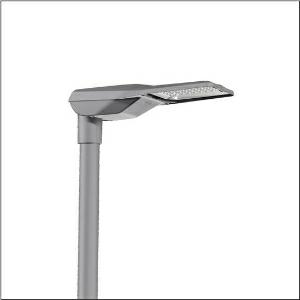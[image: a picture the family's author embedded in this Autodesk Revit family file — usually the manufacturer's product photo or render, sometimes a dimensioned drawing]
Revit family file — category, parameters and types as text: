
# Revit family: streetlight_sl_21_iq_mini___st1_5a_5xe2p31d08gb_fdd6
name_source: partatom
category: Lighting Fixtures
units: mm (PartAtom-declared; Revit-internal decimal feet)

## family parameters
Cut with Voids When Loaded = No
Host = Face
Light Source = No
Part Type = Normal
Room Calculation Point = No
Round Connector Dimension = Use Diameter
Shared = No

## types (1)
- --- (1 x LED, 5580 lm, 37.1 W, 3000K)
    Apparent Load = 37 VA
    CIE Flux Codes = 22 53 95 100 100
    Color Rendering = 70
    Color Temperature = 3000K
    Default Elevation = 1800 mm
    Description = Streetlight SL 21 iQ mini, mast luminaire, primary light control with lens, of PMMA, primary optical cover: cover, of toughened safety glass, transparent, light distribution: ST1.5a, light emission: direct distribution, primary light characteristic: asymmetric, installation type: post-top, side-entry, LED, High Power LED, rated luminous flux: 5.580lm, luminous efficacy: 150lm/W, light colour: 730, colour temperature: 3000K, control gear: iQ-Comfort, control: Auto-Match, Temp-Guard, Lumen-Switch, Night-Set, Smart-Wire, Light-Fading, Desk-Remote (wireless, voltage-free reading and setting of iQ features in the workshop via application-optimized NFC function/RFID function), optimised constant luminous flux control (CLO 2.0), pre-setting: linear dimming characteristic, mains connection: 220..240V, AC, 50/60Hz, start of lifetime: 37W, end of service life: 39W, reduction: 18W, luminaire housing, of diecast aluminium, powder-coated, Siteco® metallic grey (DB 702S), corrosivity category C5 mid according to DIN EN ISO 12944, please order mast flange separately, inclination adjustable: 0°, 5°, 10°, 15°, sealing non-destructively replaceable, multi-level sealing system, length: 628mm, width: 235mm, height: 110mm, mast flange for spigot size: 42mm (side-entry): 5XC10008XM4, 60/48mm (side-entry/post-top): 5XC10108XM2, 76/60mm (side-entry/post-top): 5XC10108XM1, mounting height: 4..8m, protection rating (complete): IP66, insulation class (complete): insulation class II (safety insulation), certification: CE, ENEC, ENEC+, VDE, impact resistance: IK10, permissible operating ambient temperature for outdoor applications: -40..+50°C, standard-compliant lighting for roads and squares, packaging unit: 1 piece

Light Distribution: ST1.5a
    Height = 110 mm
    Lamp = 1 x LED
    Lamp Light Flux = 5580 lm
    Lamp Power = 37.1 W
    Lamp count = 1
    Length = 625 mm
    Luminous efficacy = 150 lm/W
    Manufacturer = Siteco
    ModVariant = No
    Model = 5XE2P31D08GB
    Number of Poles = 1
    OnlyDefault = Yes
    Power Factor = 1
    Product Name = Streetlight SL 21 iQ mini | ST1.5a
    Product group = mast luminaire | pylon top
    ProductGroupID = 6100
    Protection Class = Protection class II
    Protection Degree = IP 66
    RLX_Detail_Level = 1
    RLX_Emergency_Light_Flux = 0 lm
    RLX_Emergency_Type = 0
    RLX_Emergency_Type_DB = No
    RlxData = <blob elided: 29877 chars, md5=20c81018>
    Socket = socket
    Standby Power = 0 W
    System Light Flux = 5580 lm
    System Power = 37 W
    Type Comments = factory setting: luminous flux: 100 % | dim-lin: 254 | 385 mA
    Type Image = l_1003519.jpg
    URL = http://relux.com
    VarID = @adj_197339
    Voltage = 0 V
    Weight = 0.00 kg
    Width = 234 mm

## geometry (parser evidence)
native form markers: Blend x4, Sweep x9
no freeform markers — native parametric forms only
